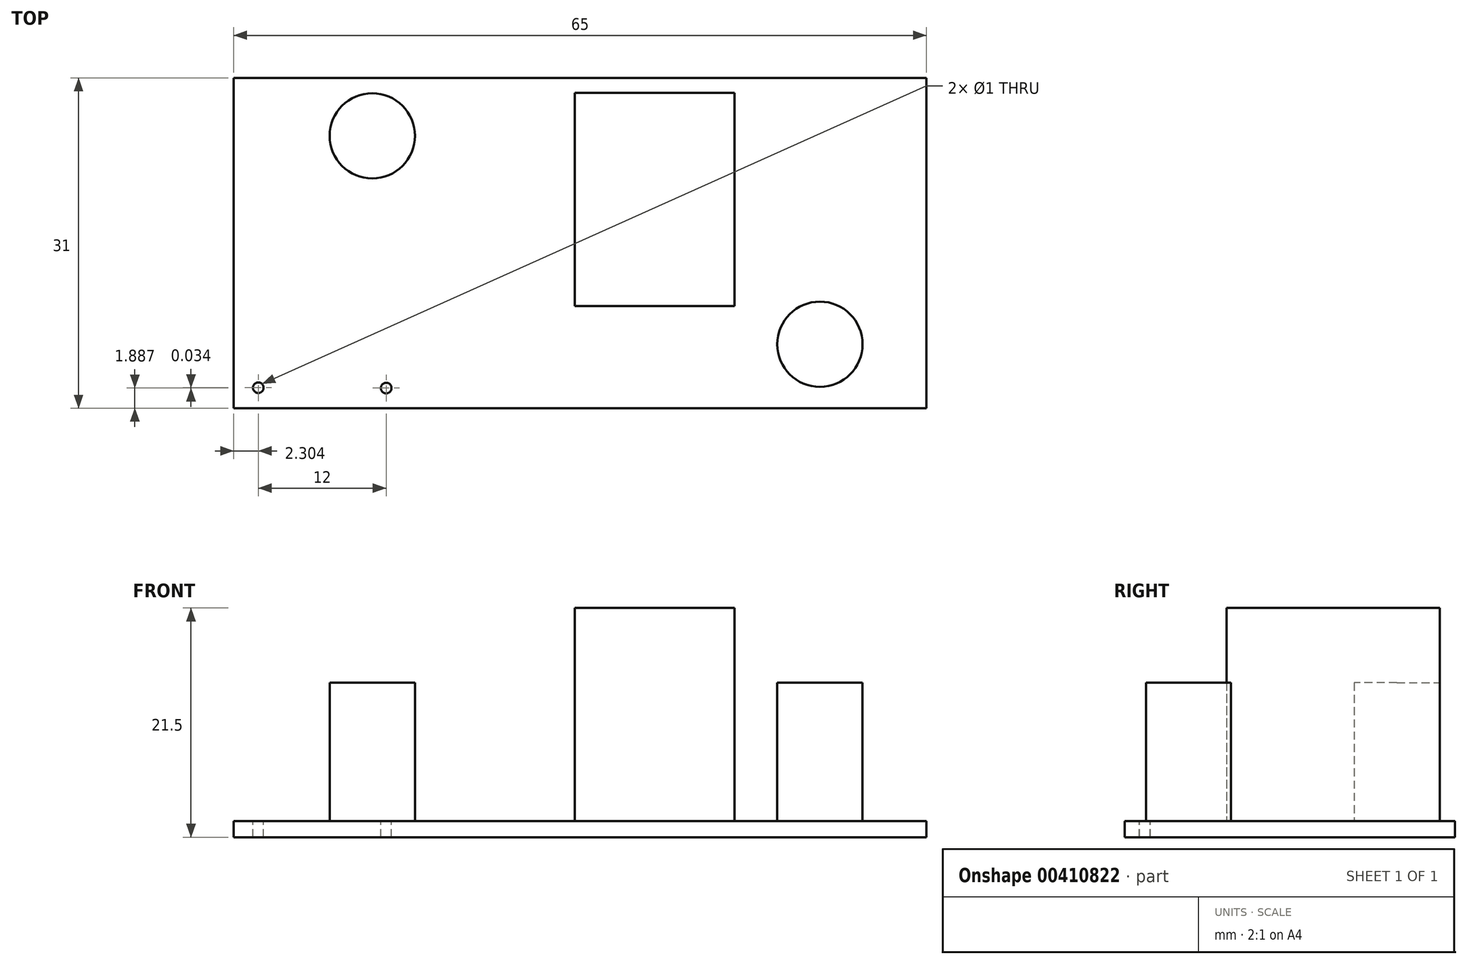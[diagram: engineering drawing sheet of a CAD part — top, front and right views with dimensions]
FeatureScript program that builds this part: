
annotation { "Feature Type Name" : "Feature", "Feature Type Description" : "" }
export const myFeature = defineFeature(function(context is Context, id is Id, definition is map)
    precondition{}
    {
        {
            var Q0;
            Q0=qCreatedBy(makeId("Front.planeOp"),FACE);
            var sketch = newSketch(context, id + "F0", { "sketchPlane" : qUnion([Q0])});
            skLineSegment(sketch, "E0.bottom", {"start": v(32.5, 0.75) * mm, "end": v(-32.5, 0.75) * mm});
            skLineSegment(sketch, "E0.top", {"start": v(32.5, -0.75) * mm, "end": v(-32.5, -0.75) * mm});
            skLineSegment(sketch, "E0.left", {"start": v(32.5, 0.75) * mm, "end": v(32.5, -0.75) * mm});
            skLineSegment(sketch, "E0.right", {"start": v(-32.5, 0.75) * mm, "end": v(-32.5, -0.75) * mm});
            skPoint(sketch, "E0.middle", {"position": v(0, 0) * mm});
            skSolve(sketch);
        }
        {
            var Q0;
            Q0 = qSketchRegion(id + "F0", true);
            extrude(context, id + "F1", {"entities" : qUnion([Q0]), "endBound" : BoundingType.SYMMETRIC, "depth" : 31 * mm});
        }
        {
            var Q0;
            Q0=makeQuery(id+"F1.opExtrude","SWEPT_FACE",FACE,{"disambiguationData":[OSD([sQuery(id+"F0.wireOp",EDGE,"E0.bottom")])]});
            var sketch = newSketch(context, id + "F2", { "sketchPlane" : qUnion([Q0])});
            skLineSegment(sketch, "E1.bottom", {"start": v(-0.5, 14.08) * mm, "end": v(14.5, 14.08) * mm});
            skLineSegment(sketch, "E1.top", {"start": v(-0.5, -5.92) * mm, "end": v(14.5, -5.92) * mm});
            skLineSegment(sketch, "E1.left", {"start": v(-0.5, 14.08) * mm, "end": v(-0.5, -5.92) * mm});
            skLineSegment(sketch, "E1.right", {"start": v(14.5, 14.08) * mm, "end": v(14.5, -5.92) * mm});
            skSolve(sketch);
        }
        {
            var Q0;
            Q0 = qSketchRegion(id + "F2", true);
            extrude(context, id + "F3", {"entities" : qUnion([Q0]), "operationType" : NewBodyOperationType.ADD, "depth" : 20 * mm});
        }
        {
            var Q0;
            Q0=makeQuery(id+"F1.opExtrude","SWEPT_FACE",FACE,{"disambiguationData":[OSD([sQuery(id+"F0.wireOp",EDGE,"E0.bottom")])]});
            var sketch = newSketch(context, id + "F4", { "sketchPlane" : qUnion([Q0])});
            skCircle(sketch, "E2", {"center": v(-19.5, 10.05) * mm, "radius": 4 * mm});
            skSolve(sketch);
        }
        {
            var Q0;
            Q0 = qSketchRegion(id + "F4", true);
            extrude(context, id + "F5", {"entities" : qUnion([Q0]), "operationType" : NewBodyOperationType.ADD, "depth" : 13 * mm});
        }
        {
            var Q0;
            Q0=makeQuery(id+"F1.opExtrude","SWEPT_FACE",FACE,{"disambiguationData":[OSD([sQuery(id+"F0.wireOp",EDGE,"E0.bottom")])]});
            var sketch = newSketch(context, id + "F6", { "sketchPlane" : qUnion([Q0])});
            skCircle(sketch, "E3", {"center": v(22.5, -9.5) * mm, "radius": 4 * mm});
            skSolve(sketch);
        }
        {
            var Q0;
            Q0 = qSketchRegion(id + "F6", true);
            extrude(context, id + "F7", {"entities" : qUnion([Q0]), "operationType" : NewBodyOperationType.ADD, "depth" : 13 * mm});
        }
        {
            var Q0;
            Q0=makeQuery(id+"F1.opExtrude","SWEPT_FACE",FACE,{"disambiguationData":[OSD([sQuery(id+"F0.wireOp",EDGE,"E0.bottom")])]});
            var sketch = newSketch(context, id + "F8", { "sketchPlane" : qUnion([Q0])});
            skCircle(sketch, "E4", {"center": v(-30.2, -13.58) * mm, "radius": 0.5 * mm});
            skSolve(sketch);
        }
        {
            var Q0;
            Q0 = qSketchRegion(id + "F8", true);
            extrude(context, id + "F9", {"entities" : qUnion([Q0]), "operationType" : NewBodyOperationType.REMOVE, "oppositeDirection" : true, "depth" : 25.4 * mm});
        }
        {
            var Q0;
            Q0=makeQuery(id+"F1.opExtrude","SWEPT_FACE",FACE,{"disambiguationData":[OSD([sQuery(id+"F0.wireOp",EDGE,"E0.bottom")])]});
            var sketch = newSketch(context, id + "F10", { "sketchPlane" : qUnion([Q0])});
            skCircle(sketch, "E5", {"center": v(-18.2, -13.61) * mm, "radius": 0.5 * mm});
            skSolve(sketch);
        }
        {
            var Q0;
            Q0 = qSketchRegion(id + "F10", true);
            extrude(context, id + "F11", {"entities" : qUnion([Q0]), "operationType" : NewBodyOperationType.REMOVE, "oppositeDirection" : true, "depth" : 25.4 * mm});
        }
    });
